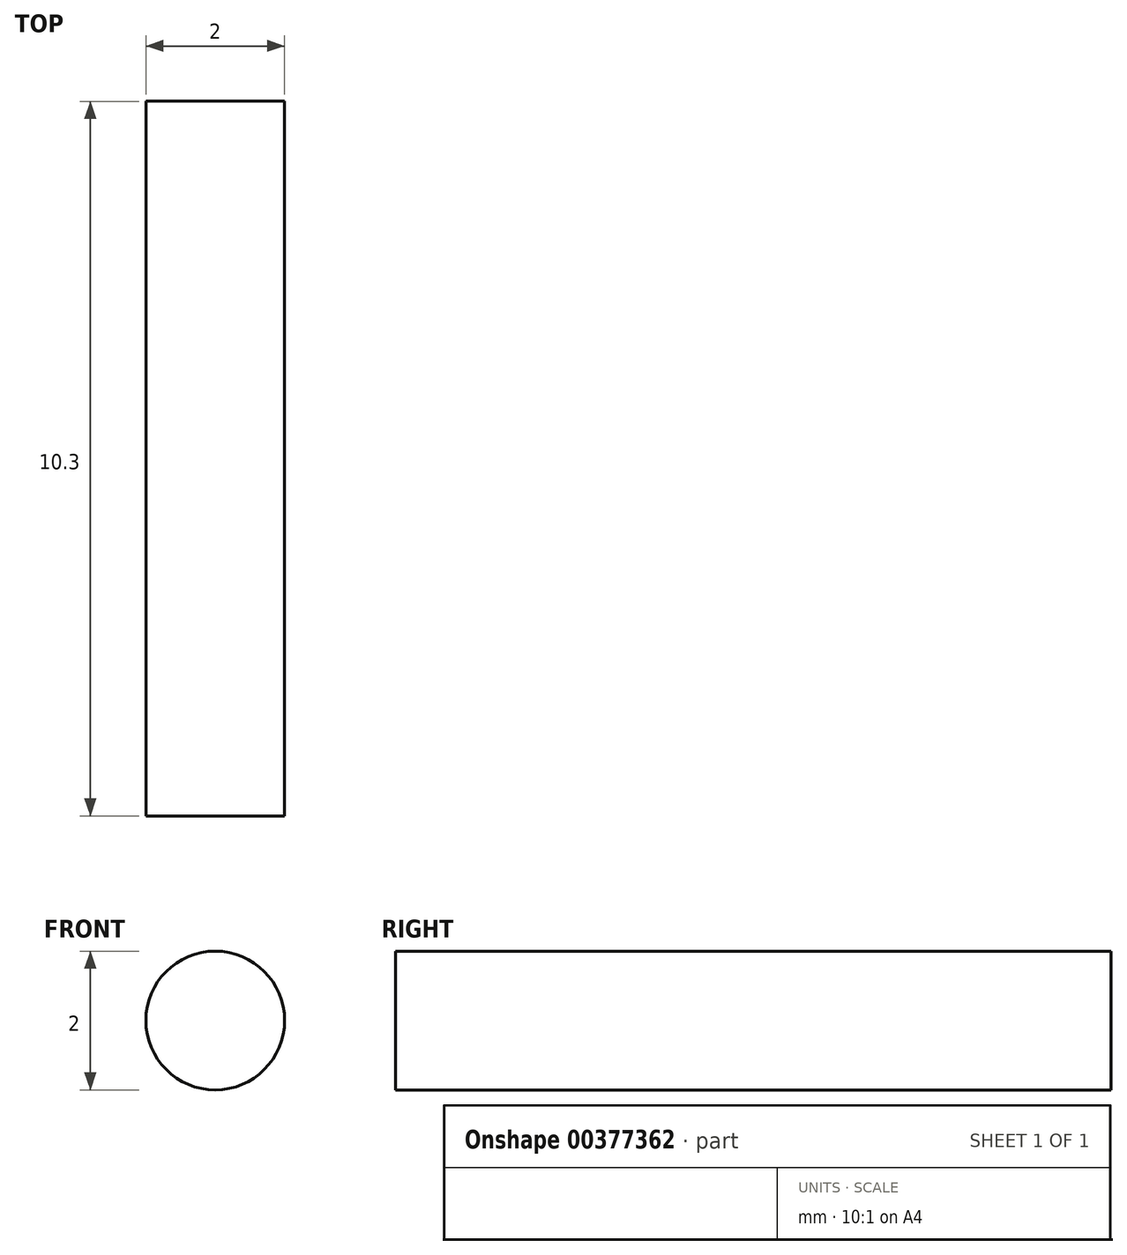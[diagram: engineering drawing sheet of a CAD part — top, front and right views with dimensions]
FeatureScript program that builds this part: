
annotation { "Feature Type Name" : "Feature", "Feature Type Description" : "" }
export const myFeature = defineFeature(function(context is Context, id is Id, definition is map)
    precondition{}
    {
        {
            var Q0;
            Q0=qCreatedBy(makeId("Front.planeOp"),FACE);
            var sketch = newSketch(context, id + "F0", { "sketchPlane" : qUnion([Q0])});
            skCircle(sketch, "E0", {"center": v(0, 0) * mm, "radius": 1 * mm});
            skSolve(sketch);
        }
        {
            var Q0;
            Q0=qSketchRegion(id+"F0",true);
            extrude(context, id + "F1", {"entities" : qUnion([Q0]), "depth" : (10.3 / 2) * mm, "hasSecondDirection" : true, "secondDirectionOppositeDirection" : true, "secondDirectionDepth" : (10.3 / 2) * mm});
        }
    });
